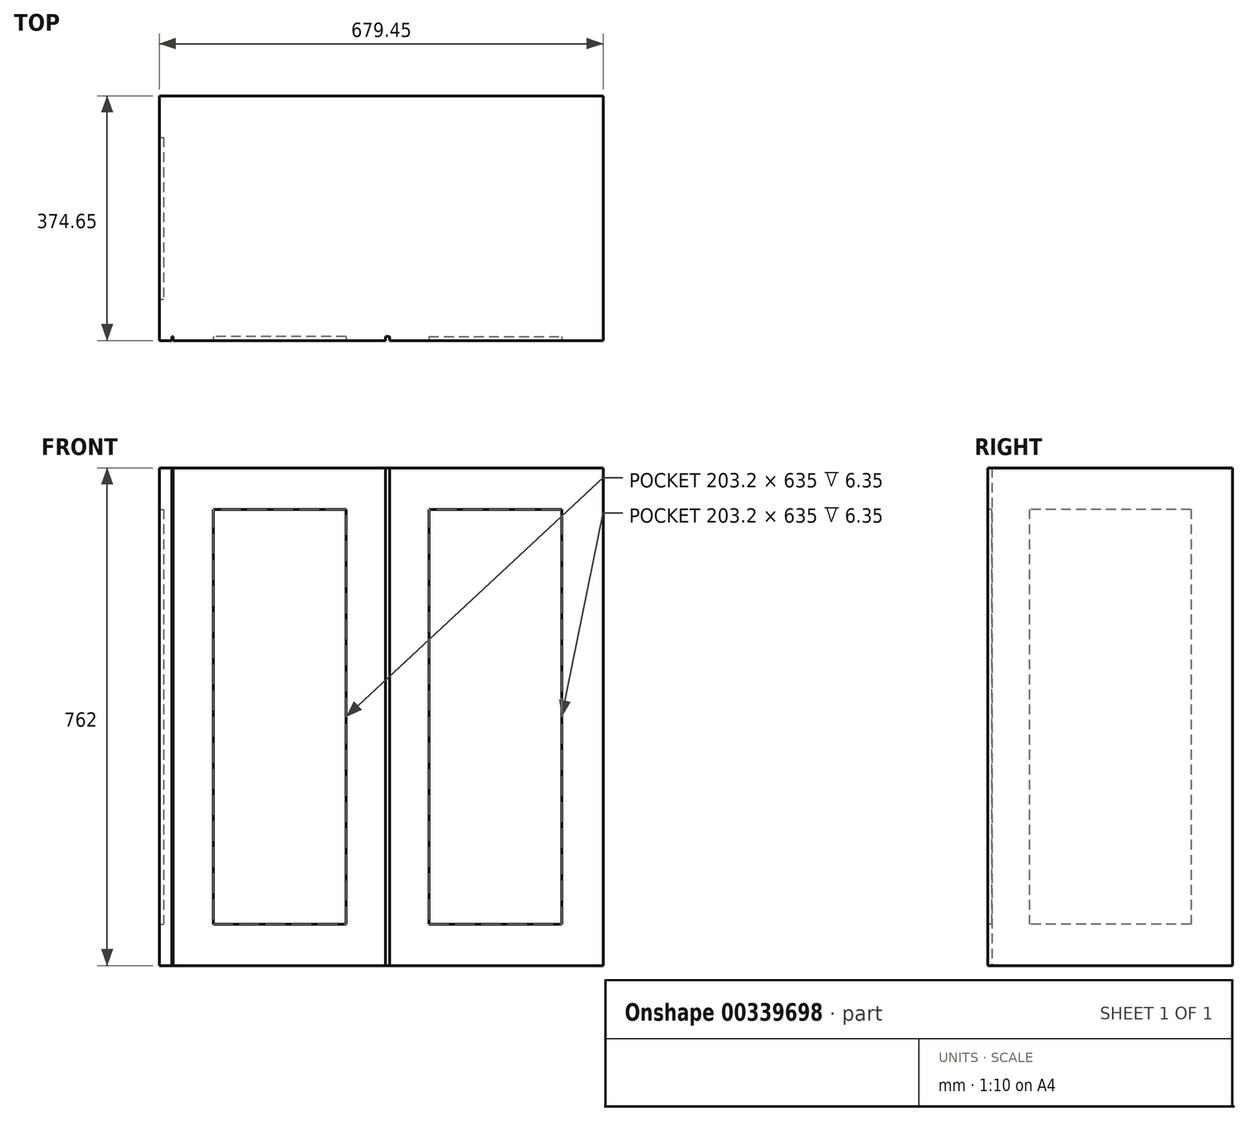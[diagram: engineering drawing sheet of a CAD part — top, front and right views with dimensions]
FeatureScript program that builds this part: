
annotation { "Feature Type Name" : "Feature", "Feature Type Description" : "" }
export const myFeature = defineFeature(function(context is Context, id is Id, definition is map)
    precondition{}
    {
        {
            var Q0;
            Q0=qCreatedBy(makeId("Front.planeOp"),FACE);
            var sketch = newSketch(context, id + "F0", { "sketchPlane" : qUnion([Q0])});
            skLineSegment(sketch, "E0.bottom", {"start": v(227.9, 0) * mm, "end": v(-102.3, 0) * mm});
            skLineSegment(sketch, "E0.top", {"start": v(227.9, 762) * mm, "end": v(-102.3, 762) * mm});
            skLineSegment(sketch, "E0.left", {"start": v(227.9, 0) * mm, "end": v(227.9, 762) * mm});
            skLineSegment(sketch, "E0.right", {"start": v(-102.3, 0) * mm, "end": v(-102.3, 762) * mm});
            skLineSegment(sketch, "E1.0", {"start": v(164.4, 698.5) * mm, "end": v(-38.8, 698.5) * mm});
            skLineSegment(sketch, "E1.1", {"start": v(164.4, 63.5) * mm, "end": v(164.4, 698.5) * mm});
            skLineSegment(sketch, "E1.2", {"start": v(164.4, 63.5) * mm, "end": v(-38.8, 63.5) * mm});
            skLineSegment(sketch, "E1.3", {"start": v(-38.8, 63.5) * mm, "end": v(-38.8, 698.5) * mm});
            skLineSegment(sketch, "E2.bottom", {"start": v(-102.3, 0) * mm, "end": v(227.9, 0) * mm});
            skLineSegment(sketch, "E3.bottom", {"start": v(-102.3, 762) * mm, "end": v(227.9, 762) * mm});
            skLineSegment(sketch, "E4.MirrorCS", {"start": v(227.9, 762) * mm, "end": v(558.1, 762) * mm});
            skLineSegment(sketch, "E5.MirrorCS", {"start": v(558.1, 762) * mm, "end": v(227.9, 762) * mm});
            skLineSegment(sketch, "E6.MirrorCS", {"start": v(227.9, 0) * mm, "end": v(558.1, 0) * mm});
            skLineSegment(sketch, "E7.MirrorCS", {"start": v(558.1, 0) * mm, "end": v(227.9, 0) * mm});
            skLineSegment(sketch, "E8.MirrorCS", {"start": v(494.6, 63.5) * mm, "end": v(494.6, 698.5) * mm});
            skLineSegment(sketch, "E9.MirrorCS", {"start": v(291.4, 63.5) * mm, "end": v(494.6, 63.5) * mm});
            skLineSegment(sketch, "E10.MirrorCS", {"start": v(291.4, 63.5) * mm, "end": v(291.4, 698.5) * mm});
            skLineSegment(sketch, "E11.MirrorCS", {"start": v(291.4, 698.5) * mm, "end": v(494.6, 698.5) * mm});
            skLineSegment(sketch, "E12.MirrorCS", {"start": v(558.1, 0) * mm, "end": v(558.1, 762) * mm});
            skLineSegment(sketch, "E13", {"start": v(224.73, 762) * mm, "end": v(224.73, 0) * mm});
            skLineSegment(sketch, "E14", {"start": v(231.08, 762) * mm, "end": v(231.08, 0) * mm});
            skLineSegment(sketch, "E15", {"start": v(-100.26, 762) * mm, "end": v(-100.26, 0) * mm});
            skSolve(sketch);
        }
        {
            var Q0;
            Q0=makeQuery(id+"F0.imprint","IMPRINT",FACE,{"disambiguationData":[TD([[makeQuery(id+"F0.imprint","IMPRINT",EDGE,{"derivedFrom":sQuery(id+"F0.wireOp",EDGE,"E1.0")}),1.0]])]});
            var Q1;
            Q1=makeQuery(id+"F0.imprint","IMPRINT",FACE,{"disambiguationData":[TD([[makeQuery(id+"F0.imprint","IMPRINT",EDGE,{"derivedFrom":sQuery(id+"F0.wireOp",EDGE,"E2.bottom")}),-1.0]])]});
            var Q2;
            Q2=makeQuery(id+"F0.imprint","IMPRINT",FACE,{"disambiguationData":[TD([[makeQuery(id+"F0.imprint","IMPRINT",EDGE,{"derivedFrom":sQuery(id+"F0.wireOp",EDGE,"E0.left")}),1.0]])]});
            var Q3;
            {var subQ0=sQuery(id+"F0.wireOp",EDGE,"E3.top");Q3=makeQuery(id+"F0.imprint","IMPRINT",FACE,{"disambiguationData":[TD([[makeQuery(id+"F0.imprint","IMPRINT",EDGE,{"derivedFrom":subQ0}),-1.0]])]});}
            var Q4;
            {var subQ0=sQuery(id+"F0.wireOp",EDGE,"E3.bottom");Q4=makeQuery(id+"F0.imprint","IMPRINT",FACE,{"disambiguationData":[TD([[makeQuery(id+"F0.imprint","IMPRINT",EDGE,{"derivedFrom":subQ0}),1.0]])]});}
            var Q5;
            Q5=makeQuery(id+"F0.imprint","IMPRINT",FACE,{"disambiguationData":[TD([[makeQuery(id+"F0.imprint","IMPRINT",EDGE,{"derivedFrom":sQuery(id+"F0.wireOp",EDGE,"E8.MirrorCS")}),1.0]])]});
            var Q6;
            {var subQ2=sQuery(id+"F0.wireOp",EDGE,"ed679ab7-f109-45c4-9ee2-0cc617b6c41517.MirrorCS");Q6=makeQuery(id+"F0.imprint","IMPRINT",FACE,{"disambiguationData":[TD([[makeQuery(id+"F0.imprint","IMPRINT",EDGE,{"derivedFrom":subQ2}),-1.0]])]});}
            var Q7;
            Q7=makeQuery(id+"F0.imprint","IMPRINT",FACE,{"disambiguationData":[TD([[makeQuery(id+"F0.imprint","IMPRINT",EDGE,{"derivedFrom":sQuery(id+"F0.wireOp",EDGE,"ed679ab7-f109-45c4-9ee2-0cc617b6c4156.MirrorCS")}),1.0]])]});
            var Q8;
            Q8=makeQuery(id+"F0.imprint","IMPRINT",FACE,{"disambiguationData":[TD([[makeQuery(id+"F0.imprint","IMPRINT",EDGE,{"derivedFrom":sQuery(id+"F0.wireOp",EDGE,"E0.left")}),-1.0]])]});
            var Q9;
            {var subQ0=sQuery(id+"F0.wireOp",EDGE,"E5.MirrorCS");Q9=makeQuery(id+"F0.imprint","IMPRINT",FACE,{"disambiguationData":[TD([[makeQuery(id+"F0.imprint","IMPRINT",EDGE,{"derivedFrom":subQ0}),-1.0]])]});}
            var Q10;
            Q10=makeQuery(id+"F0.imprint","IMPRINT",FACE,{"disambiguationData":[TD([[makeQuery(id+"F0.imprint","IMPRINT",EDGE,{"derivedFrom":sQuery(id+"F0.wireOp",EDGE,"E8.MirrorCS")}),-1.0]])]});
            var Q11;
            Q11=makeQuery(id+"F0.imprint","IMPRINT",FACE,{"disambiguationData":[TD([[makeQuery(id+"F0.imprint","IMPRINT",EDGE,{"derivedFrom":sQuery(id+"F0.wireOp",EDGE,"E1.0")}),-1.0]])]});
            var Q12;
            {var subQ0=sQuery(id+"F0.wireOp",EDGE,"E0.right");Q12=makeQuery(id+"F0.imprint","IMPRINT",FACE,{"disambiguationData":[TD([[makeQuery(id+"F0.imprint","IMPRINT",EDGE,{"derivedFrom":subQ0}),-1.0]])]});}
            extrude(context, id + "F1", {"entities" : qUnion([Q0, Q1, Q2, Q3, Q4, Q5, Q6, Q7, Q8, Q9, Q10, Q11, Q12]), "oppositeDirection" : true, "depth" : 374.65 * mm, "offsetDistance" : 25.4 * mm});
        }
        {
            var Q0;
            Q0=makeQuery(id+"F0.imprint","IMPRINT",FACE,{"disambiguationData":[TD([[makeQuery(id+"F0.imprint","IMPRINT",EDGE,{"derivedFrom":sQuery(id+"F0.wireOp",EDGE,"E1.0")}),1.0]])]});
            var Q1;
            Q1=makeQuery(id+"F0.imprint","IMPRINT",FACE,{"disambiguationData":[TD([[makeQuery(id+"F0.imprint","IMPRINT",EDGE,{"derivedFrom":sQuery(id+"F0.wireOp",EDGE,"E3.bottom")}),1.0]])]});
            var Q2;
            Q2=makeQuery(id+"F0.imprint","IMPRINT",FACE,{"disambiguationData":[TD([[makeQuery(id+"F0.imprint","IMPRINT",EDGE,{"derivedFrom":sQuery(id+"F0.wireOp",EDGE,"E8.MirrorCS")}),1.0]])]});
            var Q3;
            {var subQ0=sQuery(id+"F0.wireOp",EDGE,"E5.MirrorCS");Q3=makeQuery(id+"F0.imprint","IMPRINT",FACE,{"disambiguationData":[TD([[makeQuery(id+"F0.imprint","IMPRINT",EDGE,{"derivedFrom":subQ0}),-1.0]])]});}
            var Q4;
            {var subQ0=sQuery(id+"F0.wireOp",EDGE,"E0.left");Q4=makeQuery(id+"F0.imprint","IMPRINT",FACE,{"disambiguationData":[TD([[makeQuery(id+"F0.imprint","IMPRINT",EDGE,{"derivedFrom":subQ0}),1.0]])]});}
            var Q5;
            {var subQ0=sQuery(id+"F0.wireOp",EDGE,"E0.left");Q5=makeQuery(id+"F0.imprint","IMPRINT",FACE,{"disambiguationData":[TD([[makeQuery(id+"F0.imprint","IMPRINT",EDGE,{"derivedFrom":subQ0}),-1.0]])]});}
            var Q6;
            {var subQ0=sQuery(id+"F0.wireOp",EDGE,"E0.right");Q6=makeQuery(id+"F0.imprint","IMPRINT",FACE,{"disambiguationData":[TD([[makeQuery(id+"F0.imprint","IMPRINT",EDGE,{"derivedFrom":subQ0}),-1.0]])]});}
            extrude(context, id + "F2", {"entities" : qUnion([Q0, Q1, Q2, Q3, Q4, Q5, Q6]), "operationType" : NewBodyOperationType.REMOVE, "oppositeDirection" : true, "depth" : 6.35 * mm, "offsetDistance" : 25.4 * mm});
        }
        {
            var Q0;
            Q0=makeQuery(id+"F1.opExtrude","SWEPT_FACE",FACE,{"disambiguationData":[OSD([sQuery(id+"F0.wireOp",EDGE,"E0.right")])]});
            var sketch = newSketch(context, id + "F3", { "sketchPlane" : qUnion([Q0])});
            skLineSegment(sketch, "E16.bottom", {"start": v(-311.15, 698.5) * mm, "end": v(-63.5, 698.5) * mm});
            skLineSegment(sketch, "E16.top", {"start": v(-311.15, 63.5) * mm, "end": v(-63.5, 63.5) * mm});
            skLineSegment(sketch, "E16.left", {"start": v(-311.15, 698.5) * mm, "end": v(-311.15, 63.5) * mm});
            skLineSegment(sketch, "E16.right", {"start": v(-63.5, 698.5) * mm, "end": v(-63.5, 63.5) * mm});
            skLineSegment(sketch, "E17.bottom", {"start": v(-374.65, 762) * mm, "end": v(0, 762) * mm});
            skLineSegment(sketch, "E17.top", {"start": v(-374.65, 0) * mm, "end": v(0, 0) * mm});
            skLineSegment(sketch, "E17.left", {"start": v(-374.65, 762) * mm, "end": v(-374.65, 0) * mm});
            skLineSegment(sketch, "E17.right", {"start": v(0, 762) * mm, "end": v(0, 0) * mm});
            skSolve(sketch);
        }
        {
            var Q0;
            Q0=makeQuery(id+"F3.imprint","IMPRINT",FACE,{"disambiguationData":[TD([[makeQuery(id+"F3.imprint","IMPRINT",EDGE,{"derivedFrom":sQuery(id+"F3.wireOp",EDGE,"E16.bottom")}),1.0]])]});
            var Q1;
            {var subQ2=sQuery(id+"F3.wireOp",EDGE,"E17.right");Q1=makeQuery(id+"F3.imprint","IMPRINT",FACE,{"disambiguationData":[TD([[makeQuery(id+"F3.imprint","IMPRINT",EDGE,{"derivedFrom":subQ2}),-1.0]])]});}
            extrude(context, id + "F4", {"entities" : qUnion([Q0, Q1]), "operationType" : NewBodyOperationType.ADD, "depth" : 19.05 * mm, "offsetDistance" : 25.4 * mm});
        }
        {
            var Q0;
            Q0=makeQuery(id+"F3.imprint","IMPRINT",FACE,{"disambiguationData":[TD([[makeQuery(id+"F3.imprint","IMPRINT",EDGE,{"derivedFrom":sQuery(id+"F3.wireOp",EDGE,"E16.bottom")}),-1.0]])]});
            extrude(context, id + "F5", {"entities" : qUnion([Q0]), "operationType" : NewBodyOperationType.ADD, "depth" : 12.7 * mm, "offsetDistance" : 25.4 * mm});
        }
    });
